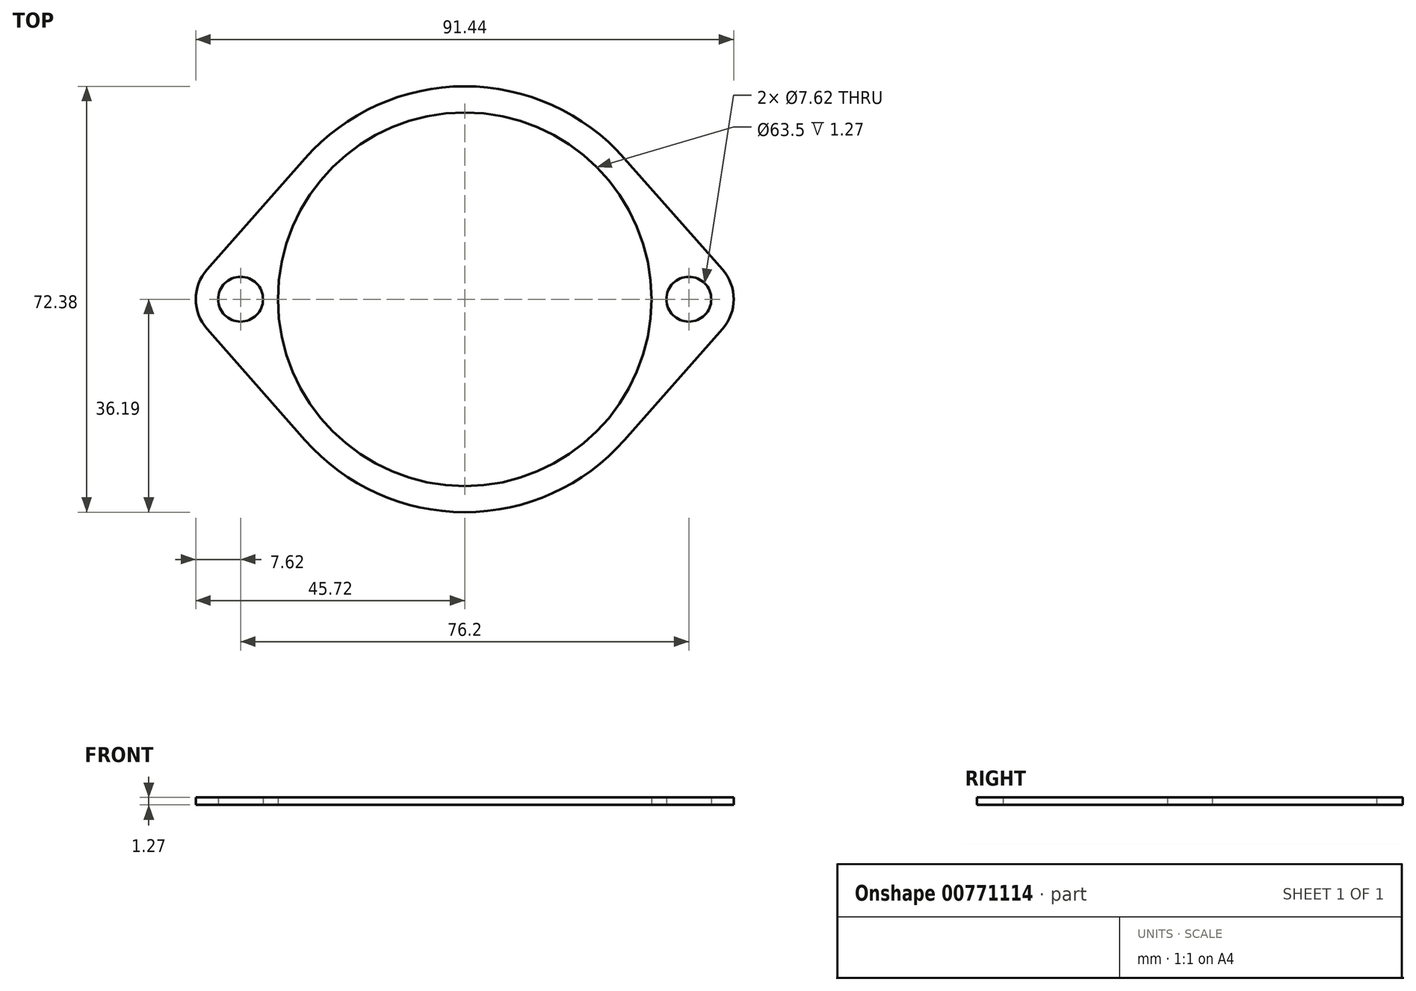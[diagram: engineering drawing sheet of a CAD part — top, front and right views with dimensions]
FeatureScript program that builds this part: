
annotation { "Feature Type Name" : "Feature", "Feature Type Description" : "" }
export const myFeature = defineFeature(function(context is Context, id is Id, definition is map)
    precondition{}
    {
        {
            var Q0;
            Q0=qCreatedBy(makeId("Top.planeOp"),FACE);
            var sketch = newSketch(context, id + "F0", { "sketchPlane" : qUnion([Q0])});
            skCircle(sketch, "E0", {"center": v(0, 0) * mm, "radius": 31.75 * mm});
            skCircle(sketch, "E1", {"center": v(38.1, 0) * mm, "radius": 3.81 * mm});
            skCircle(sketch, "E2", {"center": v(-38.1, 0) * mm, "radius": 3.81 * mm});
            skArc(sketch, "E3", {"start": v(43.82, -5.04) * mm, "mid": v(45.72, 0) * mm, "end": v(43.81, 5.04) * mm});
            skArc(sketch, "E4", {"start": v(-43.82, 5.04) * mm, "mid": v(-45.72, 0) * mm, "end": v(-43.82, -5.04) * mm});
            skLineSegment(sketch, "E5", {"start": v(-43.82, 5.04) * mm, "end": v(-27.15, 23.94) * mm});
            skLineSegment(sketch, "E6", {"start": v(27.15, 23.94) * mm, "end": v(43.81, 5.04) * mm});
            skLineSegment(sketch, "E7", {"start": v(43.82, -5.04) * mm, "end": v(27.15, -23.94) * mm});
            skLineSegment(sketch, "E8", {"start": v(-43.81, -5.04) * mm, "end": v(-27.15, -23.94) * mm});
            skArc(sketch, "E9.trimOffspring", {"start": v(-27.15, -23.94) * mm, "mid": v(0, -36.2) * mm, "end": v(27.15, -23.94) * mm});
            skArc(sketch, "E10.trimOffspring", {"start": v(27.15, 23.94) * mm, "mid": v(0, 36.2) * mm, "end": v(-27.15, 23.94) * mm});
            skSolve(sketch);
        }
        {
            var Q0;
            Q0=makeQuery(id+"F0.imprint","IMPRINT",FACE,{"disambiguationData":[TD([[makeQuery(id+"F0.imprint","IMPRINT",EDGE,{"derivedFrom":sQuery(id+"F0.wireOp",EDGE,"E0")}),-1.0]])]});
            extrude(context, id + "F1", {"entities" : qUnion([Q0]), "depth" : 1.27 * mm, "offsetDistance" : 25.4 * mm});
        }
    });
